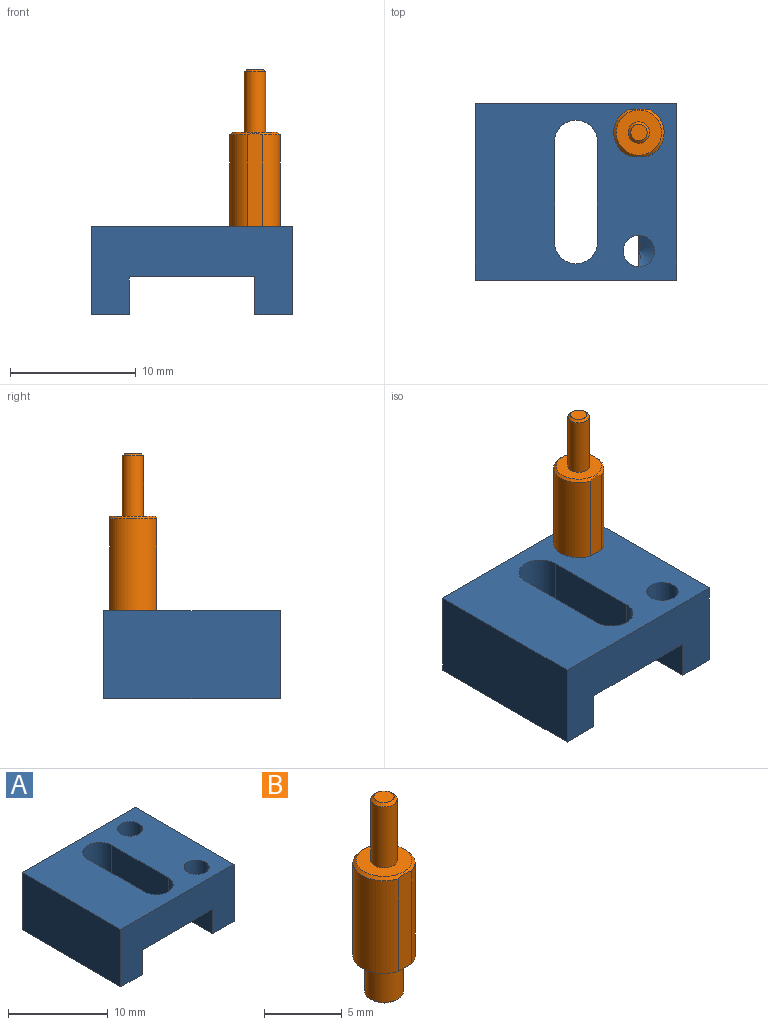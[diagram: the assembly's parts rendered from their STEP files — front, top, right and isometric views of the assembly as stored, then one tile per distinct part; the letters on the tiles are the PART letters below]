
ASSEMBLY  parts=2 mates=1
PART A: 18 faces, bbox 16x14x7 mm
  f0: plane 14x3mm, normal (-1,0,0), area 40.1mm2, adj f6,f7,f8,f9,f10,f12
  f1: plane 14x3mm, normal (1,0,0), area 42mm2, adj f2,f7,f8,f9
  f2: plane 14x3mm, normal (0,0,-1), area 42mm2, adj f1,f3,f8,f9
  f3: plane 14x7mm, normal (-1,0,0), area 98mm2, adj f2,f4,f8,f9
  f4: plane 16x14mm, normal (0,0,1), area 177.9mm2, adj f3,f5,f8,f9,f11,f13,f14,f15
  f5: plane 14x7mm, normal (1,0,0), area 98mm2, adj f4,f6,f8,f9
  f6: plane 14x3mm, normal (0,0,-1), area 42mm2, adj f0,f5,f8,f9
  f7: plane 14x10mm, normal (0,0,-1), area 98.8mm2, adj f0,f1,f8,f9,f11,f13,f14,f15
  f8: plane 16x7mm, normal (0,1,0), area 82mm2, adj f0,f1,f2,f3,f4,f5,f6,f7
  f9: plane 16x7mm, normal (0,-1,0), area 82mm2, adj f0,f1,f2,f3,f4,f5,f6,f7
  f10: cone r=0mm half-angle=59deg, axis (0,0,1), area 2.9mm2, adj f0,f11
  f11: cylinder r=1.25mm len=4mm, axis (0,0,1), area 31.4mm2, adj f4,f7,f10
  f12: cone r=0mm half-angle=59deg, axis (0,0,1), area 2.9mm2, adj f0,f13
  f13: cylinder r=1.25mm len=4mm, axis (0,0,1), area 31.4mm2, adj f4,f7,f12
  f14: plane 8x4mm, normal (1,0,0), area 32mm2, adj f4,f7,f15,f17
  f15: cylinder r=1.7mm len=4mm, axis (0,0,1), area 21.4mm2, adj f4,f7,f14,f16
  f16: plane 8x4mm, normal (-1,0,0), area 32mm2, adj f4,f7,f15,f17
  f17: cylinder r=1.7mm len=4mm, axis (0,0,1), area 21.4mm2, adj f4,f7,f14,f16
PART B: 13 faces, bbox 4x4x15.5 mm
  f0: cylinder r=2mm len=7.3mm, axis (0,0,-1), area 35.5mm2, adj f2,f3,f11,f12
  f1: cylinder r=2mm len=7.3mm, axis (0,0,-1), area 35.5mm2, adj f2,f3,f11,f12
  f2: plane 4x3.75mm, normal (0,0,-1), area 7.4mm2, adj f0,f1,f5,f11,f12
  f3: cone r=1.8mm half-angle=45deg, axis (0,0,-1), area 3mm2, adj f0,f1,f4,f11,f12
  f4: plane 3.6x3.6mm, normal (0,0,1), area 7.9mm2, adj f3,f7
  f5: cylinder r=1.25mm len=2.8mm, axis (0,0,1), area 22mm2, adj f2,f10
  f6: plane 2.1x2.1mm, normal (0,0,-1), area 3.5mm2, adj f10
  f7: cylinder r=0.85mm len=4.8mm, axis (0,0,-1), area 25.6mm2, adj f4,f9
  f8: plane 1.3x1.3mm, normal (0,0,1), area 1.3mm2, adj f9
  f9: cone r=0.65mm half-angle=45deg, axis (0,0,-1), area 1.3mm2, adj f7,f8
  f10: cone r=1.25mm half-angle=45deg, axis (0,0,1), area 2mm2, adj f5,f6
  f11: plane 7.4x1.25mm, normal (0,-1,0), area 9.2mm2, adj f0,f1,f2,f3
  f12: plane 7.45x1.52mm, normal (0,1,0), area 11.2mm2, adj f0,f1,f2,f3
PLACE A t=(34.58,-29.77,-10)mm
PLACE B t=(34.58,-29.77,-10)mm
MATE fastened A.f12 <-> B.f0  axis (0,0,1) through (154.52,34.2,7.5)mm
